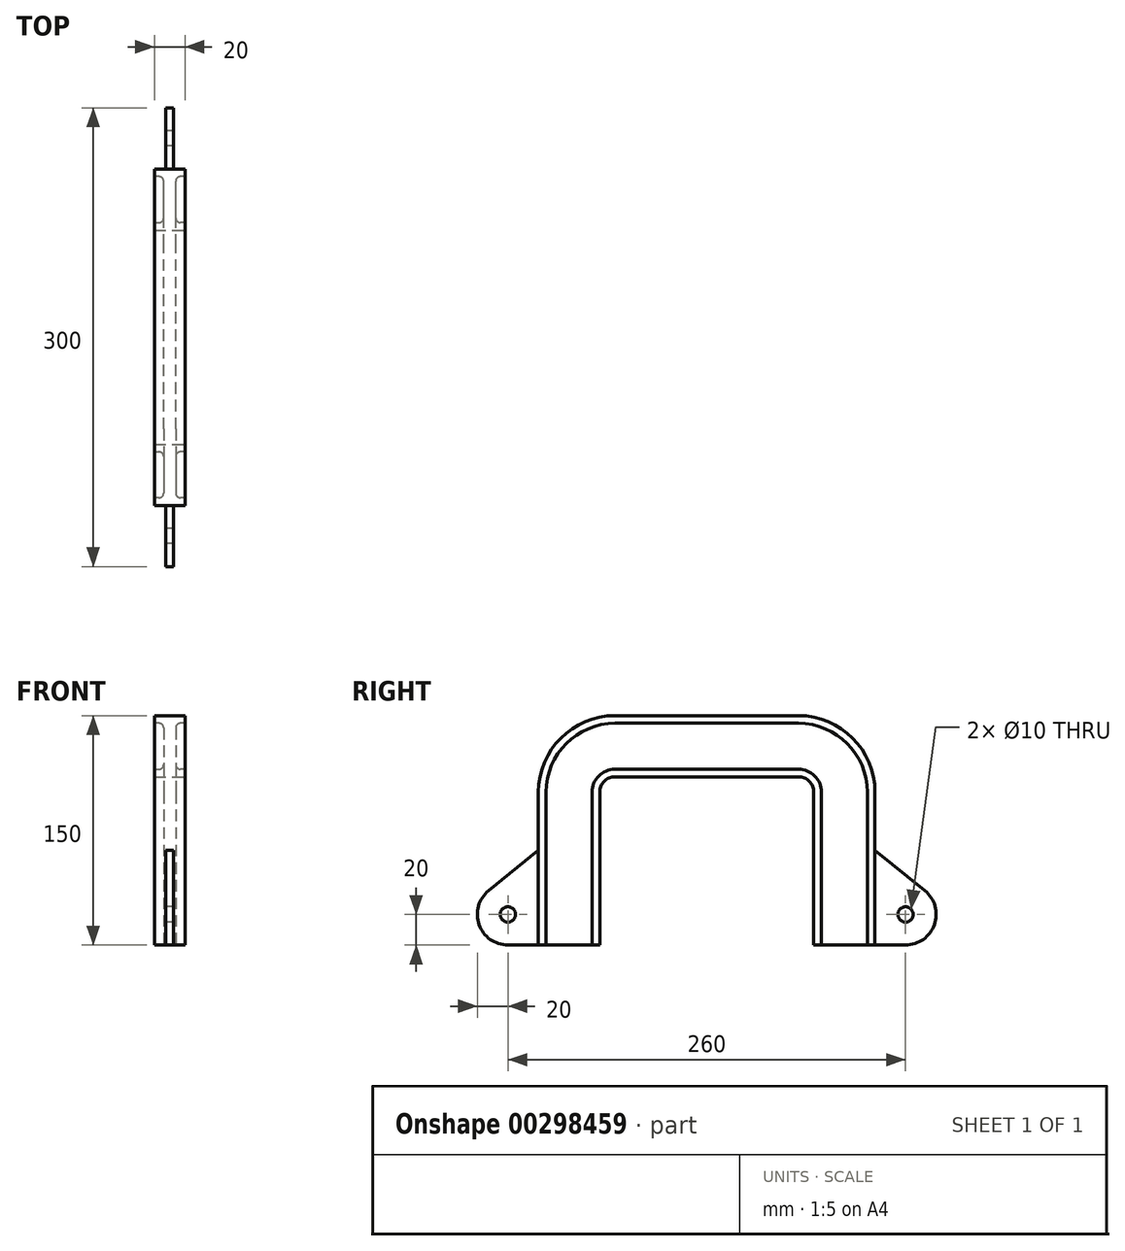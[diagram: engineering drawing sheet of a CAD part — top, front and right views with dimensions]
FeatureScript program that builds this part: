
annotation { "Feature Type Name" : "Feature", "Feature Type Description" : "" }
export const myFeature = defineFeature(function(context is Context, id is Id, definition is map)
    precondition{}
    {
        {
            var Q0;
            Q0=qCreatedBy(makeId("Front.planeOp"),FACE);
            var sketch = newSketch(context, id + "F0", { "sketchPlane" : qUnion([Q0])});
            skLineSegment(sketch, "E0", {"start": v(-10, 0) * mm, "end": v(10, 0) * mm});
            skLineSegment(sketch, "E1", {"start": v(10, 0) * mm, "end": v(10, 5) * mm});
            skLineSegment(sketch, "E2", {"start": v(10, 5) * mm, "end": v(6.97, 5) * mm});
            skLineSegment(sketch, "E3", {"start": v(-10, 0) * mm, "end": v(-10, 5) * mm});
            skLineSegment(sketch, "E4", {"start": v(-10, 5) * mm, "end": v(-6.97, 5) * mm});
            skArc(sketch, "E5", {"start": v(6.97, 5) * mm, "mid": v(4.84, 5.88) * mm, "end": v(3.97, 8) * mm});
            skArc(sketch, "E6", {"start": v(-6.97, 5) * mm, "mid": v(-4.84, 5.88) * mm, "end": v(-3.97, 8) * mm});
            skLineSegment(sketch, "E7", {"start": v(-3.97, 8) * mm, "end": v(-3.97, 32) * mm});
            skLineSegment(sketch, "E8", {"start": v(3.97, 8) * mm, "end": v(3.97, 32) * mm});
            skArc(sketch, "E9", {"start": v(-3.97, 32) * mm, "mid": v(-4.84, 34.12) * mm, "end": v(-6.97, 35) * mm});
            skArc(sketch, "E10", {"start": v(3.97, 32) * mm, "mid": v(4.84, 34.12) * mm, "end": v(6.97, 35) * mm});
            skLineSegment(sketch, "E11", {"start": v(-6.97, 35) * mm, "end": v(-10, 35) * mm});
            skLineSegment(sketch, "E12", {"start": v(-10, 35) * mm, "end": v(-10, 40) * mm});
            skLineSegment(sketch, "E13", {"start": v(-10, 40) * mm, "end": v(10, 40) * mm});
            skLineSegment(sketch, "E14", {"start": v(10, 40) * mm, "end": v(10, 35) * mm});
            skLineSegment(sketch, "E15", {"start": v(10, 35) * mm, "end": v(6.97, 35) * mm});
            skSolve(sketch);
        }
        {
            var Q0;
            Q0=qCreatedBy(makeId("Right.planeOp"),FACE);
            var sketch = newSketch(context, id + "F1", { "sketchPlane" : qUnion([Q0])});
            skLineSegment(sketch, "E16", {"start": v(0, 0) * mm, "end": v(60, 0) * mm});
            skArc(sketch, "E17", {"start": v(60, 0) * mm, "mid": v(67.07, -2.93) * mm, "end": v(70, -10) * mm});
            skLineSegment(sketch, "E18", {"start": v(70, -10) * mm, "end": v(70, -110) * mm});
            skSolve(sketch);
        }
        {
            var Q0;
            Q0 = qSketchRegion(id + "F0", true);
            var Q1;
            Q1 = qConstructionFilter(qBodyType(qCreatedBy(id + "F1" ,EDGE), BodyType.WIRE), ConstructionObject.NO);
            sweep(context, id + "F2", {"profiles" : qUnion([Q0]), "path" : qUnion([Q1])});
        }
        {
            var Q0;
            Q0=makeQuery(id+"F2.opSweep","SWEPT_BODY",BODY,{"disambiguationData":[OSD([sQuery(id+"F0.wireOp",EDGE,"E0"),sQuery(id+"F0.wireOp",EDGE,"E1"),sQuery(id+"F0.wireOp",EDGE,"E2"),sQuery(id+"F0.wireOp",EDGE,"E3"),sQuery(id+"F0.wireOp",EDGE,"E4"),sQuery(id+"F0.wireOp",EDGE,"E5"),sQuery(id+"F0.wireOp",EDGE,"E6"),sQuery(id+"F0.wireOp",EDGE,"E7"),sQuery(id+"F0.wireOp",EDGE,"E8"),sQuery(id+"F0.wireOp",EDGE,"E9"),sQuery(id+"F0.wireOp",EDGE,"E10"),sQuery(id+"F0.wireOp",EDGE,"E11"),sQuery(id+"F0.wireOp",EDGE,"E12"),sQuery(id+"F0.wireOp",EDGE,"E13"),sQuery(id+"F0.wireOp",EDGE,"E14"),sQuery(id+"F0.wireOp",EDGE,"E15"),sQuery(id+"F1.wireOp",EDGE,"E18")])]});
            var Q1;
            Q1=qCreatedBy(makeId("Front.planeOp"),FACE);
            mirror(context, id + "F3", {"operationType" : NewBodyOperationType.ADD, "entities" : qUnion([Q0]), "mirrorPlane" : qUnion([Q1])});
        }
        {
            var Q0;
            Q0=qCreatedBy(makeId("Right.planeOp"),FACE);
            var sketch = newSketch(context, id + "F4", { "sketchPlane" : qUnion([Q0])});
            skLineSegment(sketch, "E19", {"start": v(100, -110) * mm, "end": v(130, -110) * mm});
            skArc(sketch, "E20", {"start": v(130, -110) * mm, "mid": v(148.85, -96.67) * mm, "end": v(142.58, -74.45) * mm});
            skLineSegment(sketch, "E21", {"start": v(142.58, -74.45) * mm, "end": v(100, -40) * mm});
            skLineSegment(sketch, "E22", {"start": v(100, -40) * mm, "end": v(100, -110) * mm});
            skCircle(sketch, "E23", {"center": v(130, -90) * mm, "radius": 5 * mm});
            skSolve(sketch);
        }
        {
            var Q0;
            Q0=makeQuery(id+"F4.imprint","IMPRINT",FACE,{"disambiguationData":[TD([[makeQuery(id+"F4.imprint","IMPRINT",EDGE,{"derivedFrom":sQuery(id+"F4.wireOp",EDGE,"E19")}),1.0]])]});
            extrude(context, id + "F5", {"entities" : qUnion([Q0]), "operationType" : NewBodyOperationType.ADD, "endBound" : BoundingType.SYMMETRIC, "depth" : 5 * mm});
        }
        {
            var Q0;
            Q0=makeQuery(id+"F2.opSweep","SWEPT_BODY",BODY,{"disambiguationData":[OSD([sQuery(id+"F0.wireOp",EDGE,"E0"),sQuery(id+"F0.wireOp",EDGE,"E1"),sQuery(id+"F0.wireOp",EDGE,"E2"),sQuery(id+"F0.wireOp",EDGE,"E3"),sQuery(id+"F0.wireOp",EDGE,"E4"),sQuery(id+"F0.wireOp",EDGE,"E5"),sQuery(id+"F0.wireOp",EDGE,"E6"),sQuery(id+"F0.wireOp",EDGE,"E7"),sQuery(id+"F0.wireOp",EDGE,"E8"),sQuery(id+"F0.wireOp",EDGE,"E9"),sQuery(id+"F0.wireOp",EDGE,"E10"),sQuery(id+"F0.wireOp",EDGE,"E11"),sQuery(id+"F0.wireOp",EDGE,"E12"),sQuery(id+"F0.wireOp",EDGE,"E13"),sQuery(id+"F0.wireOp",EDGE,"E14"),sQuery(id+"F0.wireOp",EDGE,"E15"),sQuery(id+"F1.wireOp",EDGE,"E18")])]});
            var Q1;
            Q1=qCreatedBy(makeId("Front.planeOp"),FACE);
            mirror(context, id + "F6", {"operationType" : NewBodyOperationType.ADD, "entities" : qUnion([Q0]), "mirrorPlane" : qUnion([Q1])});
        }
    });
